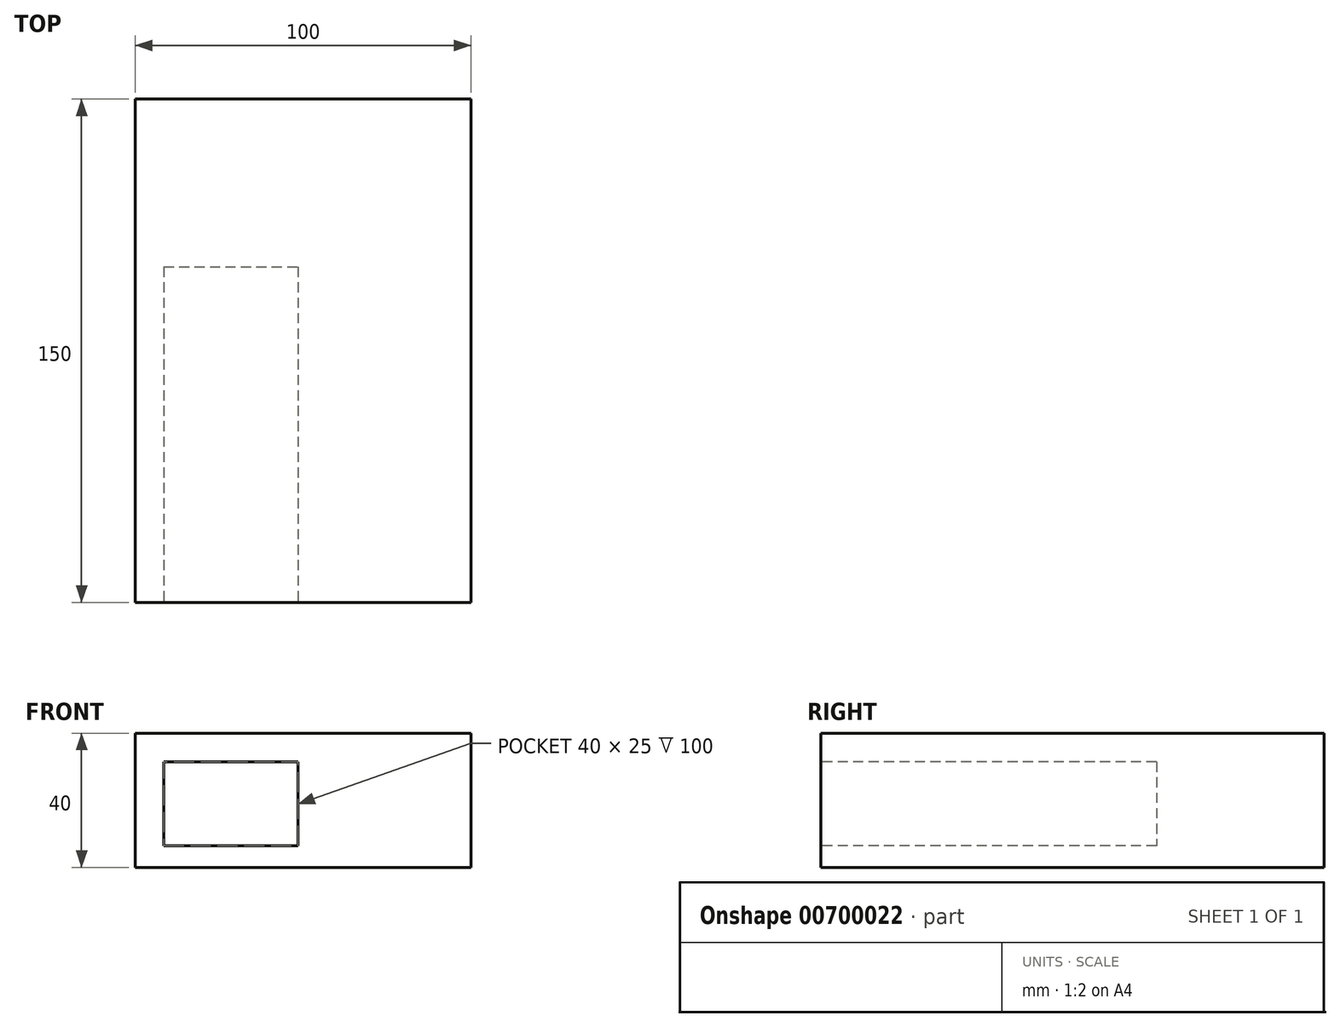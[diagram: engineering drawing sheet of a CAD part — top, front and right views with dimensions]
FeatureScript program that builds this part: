
annotation { "Feature Type Name" : "Feature", "Feature Type Description" : "" }
export const myFeature = defineFeature(function(context is Context, id is Id, definition is map)
    precondition{}
    {
        {
            var Q0;
            Q0=qCreatedBy(makeId("Top.planeOp"),FACE);
            var sketch = newSketch(context, id + "F0", { "sketchPlane" : qUnion([Q0])});
            skLineSegment(sketch, "E0.bottom", {"start": v(50, -75) * mm, "end": v(-50, -75) * mm});
            skLineSegment(sketch, "E0.top", {"start": v(50, 75) * mm, "end": v(-50, 75) * mm});
            skLineSegment(sketch, "E0.left", {"start": v(50, -75) * mm, "end": v(50, 75) * mm});
            skLineSegment(sketch, "E0.right", {"start": v(-50, -75) * mm, "end": v(-50, 75) * mm});
            skPoint(sketch, "E0.middle", {"position": v(0, 0) * mm});
            skSolve(sketch);
        }
        {
            var Q0;
            Q0 = qSketchRegion(id + "F0", true);
            extrude(context, id + "F1", {"entities" : qUnion([Q0]), "depth" : 40 * mm, "offsetDistance" : 25 * mm});
        }
        {
            var Q0;
            Q0=makeQuery(id+"F1.opExtrude","SWEPT_FACE",FACE,{"disambiguationData":[OSD([sQuery(id+"F0.wireOp",EDGE,"E0.bottom")])]});
            var sketch = newSketch(context, id + "F2", { "sketchPlane" : qUnion([Q0])});
            skLineSegment(sketch, "E1.bottom", {"start": v(-41.56, 31.43) * mm, "end": v(-1.56, 31.43) * mm});
            skLineSegment(sketch, "E1.top", {"start": v(-41.56, 6.43) * mm, "end": v(-1.56, 6.43) * mm});
            skLineSegment(sketch, "E1.left", {"start": v(-41.56, 31.43) * mm, "end": v(-41.56, 6.43) * mm});
            skLineSegment(sketch, "E1.right", {"start": v(-1.56, 31.43) * mm, "end": v(-1.56, 6.43) * mm});
            skSolve(sketch);
        }
        {
            var Q0;
            Q0 = qSketchRegion(id + "F2", true);
            extrude(context, id + "F3", {"entities" : qUnion([Q0]), "operationType" : NewBodyOperationType.REMOVE, "oppositeDirection" : true, "depth" : 100 * mm, "offsetDistance" : 25 * mm});
        }
    });
